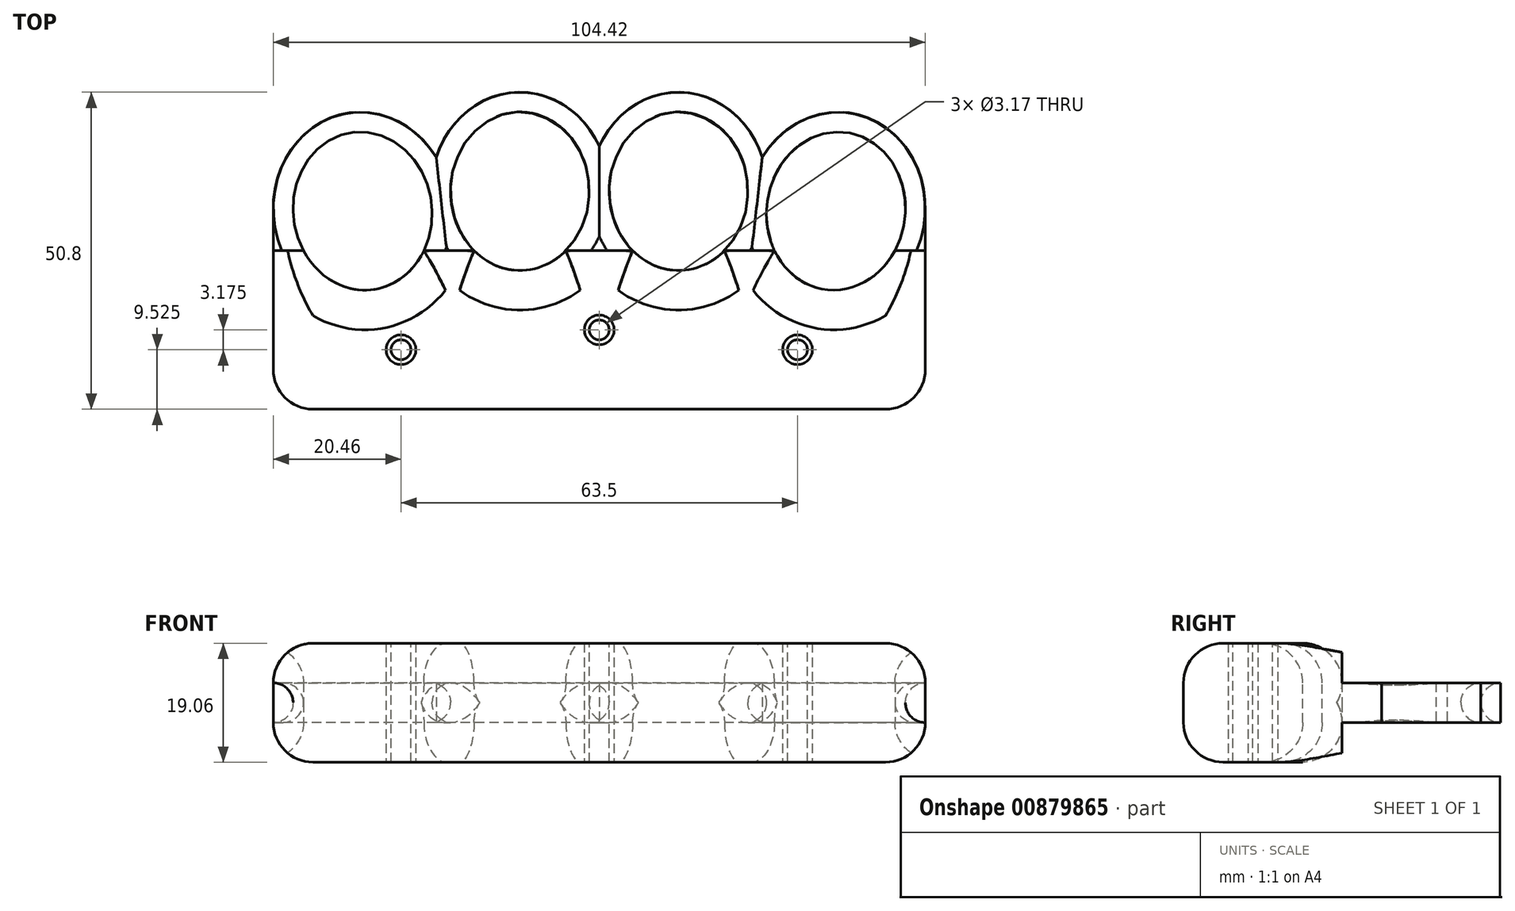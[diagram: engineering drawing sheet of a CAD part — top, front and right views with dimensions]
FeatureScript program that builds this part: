
annotation { "Feature Type Name" : "Feature", "Feature Type Description" : "" }
export const myFeature = defineFeature(function(context is Context, id is Id, definition is map)
    precondition{}
    {
        {
            var Q0;
            Q0=qCreatedBy(makeId("Top.planeOp"),FACE);
            var sketch = newSketch(context, id + "F0", { "sketchPlane" : qUnion([Q0])});
            skLineSegment(sketch, "E0.bottom", {"start": v(52.39, 0) * mm, "end": v(-52.39, 0) * mm});
            skLineSegment(sketch, "E0.top", {"start": v(52.39, 50.8) * mm, "end": v(-52.39, 50.8) * mm, "construction": true});
            skLineSegment(sketch, "E0.left", {"start": v(52.39, 0) * mm, "end": v(52.39, 50.8) * mm, "construction": true});
            skLineSegment(sketch, "E0.right", {"start": v(-52.39, 0) * mm, "end": v(-52.39, 50.8) * mm, "construction": true});
            skPoint(sketch, "E0.middle", {"position": v(0, 25.4) * mm});
            skEllipse(sketch, "E1", {"center": v(12.7, 34.93) * mm, "majorRadius": 12.7 * mm, "minorRadius": 11.11 * mm, "majorAxis": v(0, -1)});
            skEllipse(sketch, "E2", {"center": v(37.9, 31.75) * mm, "majorRadius": 12.7 * mm, "minorRadius": 11.11 * mm, "majorAxis": v(-0.13, -1)});
            skLineSegment(sketch, "E3", {"start": v(12.7, 34.93) * mm, "end": v(37.9, 31.75) * mm, "construction": true});
            skLineSegment(sketch, "E4", {"start": v(39.49, 44.35) * mm, "end": v(36.31, 19.15) * mm, "construction": true});
            skLineSegment(sketch, "E5", {"start": v(0, -19.1) * mm, "end": v(0, 88.95) * mm, "construction": true});
            skEllipticalArc(sketch, "E6", {});
            skEllipticalArc(sketch, "E7", {});
            skLineSegment(sketch, "E8", {"start": v(39.89, 47.5) * mm, "end": v(35.92, 16) * mm, "construction": true});
            skEllipticalArc(sketch, "E9.trimOffspring", {});
            skEllipticalArc(sketch, "E10.trimOffspring", {});
            skEllipticalArc(sketch, "E11.MirrorCS", {});
            skEllipse(sketch, "E12.MirrorC", {"center": v(-12.7, 34.93) * mm, "majorRadius": 12.7 * mm, "minorRadius": 11.11 * mm, "majorAxis": v(0, -1)});
            skEllipticalArc(sketch, "E13.MirrorCS", {});
            skEllipse(sketch, "E14.MirrorC", {"center": v(-37.9, 31.75) * mm, "majorRadius": 12.7 * mm, "minorRadius": 11.11 * mm, "majorAxis": v(0.13, -1)});
            skPoint(sketch, "E15.MirrorCS.end.orphan", {"position": v(-59.92, 0) * mm});
            skPoint(sketch, "E15.MirrorCS.start.orphan", {"position": v(-52.2, 31.75) * mm});
            skPoint(sketch, "E16.end.orphan", {"position": v(59.92, 0) * mm});
            skLineSegment(sketch, "E17", {"start": v(52.2, 31.75) * mm, "end": v(52.2, 0) * mm});
            skLineSegment(sketch, "E18", {"start": v(-52.2, 31.75) * mm, "end": v(-52.2, 0) * mm});
            skLineSegment(sketch, "E19.top", {"start": v(52.2, 0) * mm, "end": v(-52.2, 0) * mm, "construction": true});
            skLineSegment(sketch, "E19.left", {"start": v(52.2, 22.23) * mm, "end": v(52.2, 0) * mm, "construction": true});
            skLineSegment(sketch, "E19.right", {"start": v(-52.2, 22.23) * mm, "end": v(-52.2, 0) * mm, "construction": true});
            skPoint(sketch, "E19.middle", {"position": v(0, 11.11) * mm});
            skPoint(sketch, "E19.cornerSnap0", {"position": v(12.7, 22.23) * mm});
            skLineSegment(sketch, "E20", {"start": v(-52.2, 25.4) * mm, "end": v(-47.35, 25.4) * mm});
            skLineSegment(sketch, "E21", {"start": v(-28.08, 25.4) * mm, "end": v(-20.05, 25.4) * mm});
            skLineSegment(sketch, "E22", {"start": v(-5.35, 25.4) * mm, "end": v(5.35, 25.4) * mm});
            skLineSegment(sketch, "E23", {"start": v(20.05, 25.4) * mm, "end": v(28.08, 25.4) * mm});
            skLineSegment(sketch, "E24", {"start": v(47.35, 25.4) * mm, "end": v(52.2, 25.4) * mm});
            const initialGuessF0  = {"E6": [0.0127, 0.034925, 0, 1, 0.015875, 0.014287500000000002, 4.549107403088378, 4.626167916825997], "E7": [0.037900781237890244, 0.03175, -0.125, -0.9921567416492215, 0.015875, 0.014287500000000002, 1.6837034290787396, 4.24838283304531], "E9.trimOffspring": [0.037900781237890244, 0.03175, -0.125, -0.9921567416492215, 0.015875, 0.014287500000000002, 4.688269598477033, 4.765675536865148], "E10.trimOffspring": [0.0127, 0.034925, 0, 1, 0.015875, 0.014287500000000002, 5.064232675246107, 1.094914077134481], "E11.MirrorCS": [-0.0127, 0.034925, 0, 1, 0.015875, 0.014287500000000002, 5.188271230045105, 1.2189526319334796], "E13.MirrorCS": [-0.037900781237890244, 0.03175, 0.125, -0.9921567416492215, 0.015875, 0.014287500000000002, 2.034802474134276, 4.599481878100846]};
            skSetInitialGuess(sketch, initialGuessF0);
            skSolve(sketch);
        }
        {
            var Q0;
            {var subQ0=sQuery(id+"F0.wireOp",EDGE,"E7");Q0=makeQuery(id+"F0.imprint","IMPRINT",FACE,{"disambiguationData":[TD([[makeQuery(id+"F0.imprint","IMPRINT",EDGE,{"derivedFrom":subQ0}),1.0]])]});}
            var Q1;
            {var subQ3=sQuery(id+"F0.wireOp",EDGE,"E19.bottom");Q1=makeQuery(id+"F0.imprint","IMPRINT",FACE,{"disambiguationData":[TD([[makeQuery(id+"F0.imprint","IMPRINT",EDGE,{"derivedFrom":subQ3}),1.0]])]});}
            extrude(context, id + "F1", {"entities" : qUnion([Q0, Q1]), "depth" : 3.17 * mm, "offsetDistance" : 25.4 * mm, "hasSecondDirection" : true, "secondDirectionOppositeDirection" : true, "secondDirectionDepth" : 3.17 * mm});
        }
        {
            var Q0;
            {var subQ2=sQuery(id+"F0.wireOp",EDGE,"E20");Q0=makeQuery(id+"F0.imprint","IMPRINT",FACE,{"disambiguationData":[TD([[makeQuery(id+"F0.imprint","IMPRINT",EDGE,{"derivedFrom":subQ2}),-1.0]])]});}
            extrude(context, id + "F2", {"entities" : qUnion([Q0]), "operationType" : NewBodyOperationType.ADD, "depth" : 9.52 * mm, "offsetDistance" : 25.4 * mm, "hasSecondDirection" : true, "secondDirectionOppositeDirection" : true, "secondDirectionDepth" : 9.52 * mm});
        }
        {
            var Q0;
            Q0=makeQuery(id+"F2.opExtrude","CAP_FACE",FACE,{"disambiguationData":[OSD([sQuery(id+"F0.wireOp",EDGE,"E0.bottom"),sQuery(id+"F0.wireOp",EDGE,"E1"),sQuery(id+"F0.wireOp",EDGE,"E2"),sQuery(id+"F0.wireOp",EDGE,"E12.MirrorC"),sQuery(id+"F0.wireOp",EDGE,"E14.MirrorC"),sQuery(id+"F0.wireOp",EDGE,"E17"),sQuery(id+"F0.wireOp",EDGE,"E18"),sQuery(id+"F0.wireOp",EDGE,"E20"),sQuery(id+"F0.wireOp",EDGE,"E21"),sQuery(id+"F0.wireOp",EDGE,"E22"),sQuery(id+"F0.wireOp",EDGE,"E23"),sQuery(id+"F0.wireOp",EDGE,"E24")])],"isStart":false});
            var Q1;
            Q1=makeQuery(id+"F2.opExtrude","CAP_FACE",FACE,{"disambiguationData":[OSD([sQuery(id+"F0.wireOp",EDGE,"E0.bottom"),sQuery(id+"F0.wireOp",EDGE,"E1"),sQuery(id+"F0.wireOp",EDGE,"E2"),sQuery(id+"F0.wireOp",EDGE,"E12.MirrorC"),sQuery(id+"F0.wireOp",EDGE,"E14.MirrorC"),sQuery(id+"F0.wireOp",EDGE,"E17"),sQuery(id+"F0.wireOp",EDGE,"E18"),sQuery(id+"F0.wireOp",EDGE,"E20"),sQuery(id+"F0.wireOp",EDGE,"E21"),sQuery(id+"F0.wireOp",EDGE,"E22"),sQuery(id+"F0.wireOp",EDGE,"E23"),sQuery(id+"F0.wireOp",EDGE,"E24")])],"isStart":true});
            fillet(context, id + "F3", {"entities" : qUnion([Q0, Q1]), "radius" : 6.35 * mm, "tangentPropagation" : true, "allowEdgeOverflow" : false});
        }
        {
            var Q0;
            Q0=makeQuery(id+"F2.opExtrude","SWEPT_EDGE",EDGE,{"disambiguationData":[OSD([sQuery(id+"F0.wireOp",EDGE,"E0.bottom"),sQuery(id+"F0.wireOp",EDGE,"E17")])]});
            var Q1;
            Q1=makeQuery(id+"F2.opExtrude","SWEPT_EDGE",EDGE,{"disambiguationData":[OSD([sQuery(id+"F0.wireOp",EDGE,"E0.bottom"),sQuery(id+"F0.wireOp",EDGE,"E18")])]});
            fillet(context, id + "F4", {"entities" : qUnion([Q0, Q1]), "radius" : 6.35 * mm, "tangentPropagation" : true, "allowEdgeOverflow" : false});
        }
        {
            var Q0;
            Q0=qCreatedBy(makeId("Top.planeOp"),FACE);
            var sketch = newSketch(context, id + "F5", { "sketchPlane" : qUnion([Q0])});
            skCircle(sketch, "E25", {"center": v(0, 12.7) * mm, "radius": 1.59 * mm});
            skCircle(sketch, "E26", {"center": v(0, 12.7) * mm, "radius": 2.38 * mm});
            skCircle(sketch, "E27", {"center": v(31.75, 9.53) * mm, "radius": 1.59 * mm});
            skCircle(sketch, "E28", {"center": v(31.75, 9.53) * mm, "radius": 2.38 * mm});
            skCircle(sketch, "E29", {"center": v(-31.75, 9.52) * mm, "radius": 1.59 * mm});
            skCircle(sketch, "E30", {"center": v(-31.75, 9.52) * mm, "radius": 2.38 * mm});
            skSolve(sketch);
        }
        {
            var Q0;
            Q0=makeQuery(id+"F5.imprint","IMPRINT",FACE,{"disambiguationData":[TD([[makeQuery(id+"F5.imprint","IMPRINT",EDGE,{"derivedFrom":sQuery(id+"F5.wireOp",EDGE,"E25")}),1.0]])]});
            extrude(context, id + "F6", {"entities" : qUnion([Q0]), "operationType" : NewBodyOperationType.REMOVE, "oppositeDirection" : true, "depth" : 25.4 * mm, "offsetDistance" : 25.4 * mm, "hasSecondDirection" : true, "secondDirectionOppositeDirection" : false, "secondDirectionDepth" : 25.4 * mm});
        }
        {
            var Q0;
            Q0=makeQuery(id+"F5.imprint","IMPRINT",FACE,{"disambiguationData":[TD([[makeQuery(id+"F5.imprint","IMPRINT",EDGE,{"derivedFrom":sQuery(id+"F5.wireOp",EDGE,"E29")}),1.0]])]});
            var Q1;
            Q1=makeQuery(id+"F5.imprint","IMPRINT",FACE,{"disambiguationData":[TD([[makeQuery(id+"F5.imprint","IMPRINT",EDGE,{"derivedFrom":sQuery(id+"F5.wireOp",EDGE,"E27")}),1.0]])]});
            extrude(context, id + "F7", {"entities" : qUnion([Q0, Q1]), "operationType" : NewBodyOperationType.REMOVE, "oppositeDirection" : true, "depth" : 25.4 * mm, "offsetDistance" : 25.4 * mm, "hasSecondDirection" : true, "secondDirectionOppositeDirection" : false, "secondDirectionDepth" : 25.4 * mm});
        }
        {
            var Q0;
            Q0=makeQuery(id+"F5.imprint","IMPRINT",FACE,{"disambiguationData":[TD([[makeQuery(id+"F5.imprint","IMPRINT",EDGE,{"derivedFrom":sQuery(id+"F5.wireOp",EDGE,"E29")}),1.0]])]});
            var Q1;
            Q1=makeQuery(id+"F5.imprint","IMPRINT",FACE,{"disambiguationData":[TD([[makeQuery(id+"F5.imprint","IMPRINT",EDGE,{"derivedFrom":sQuery(id+"F5.wireOp",EDGE,"E29")}),-1.0]])]});
            var Q2;
            Q2=makeQuery(id+"F5.imprint","IMPRINT",FACE,{"disambiguationData":[TD([[makeQuery(id+"F5.imprint","IMPRINT",EDGE,{"derivedFrom":sQuery(id+"F5.wireOp",EDGE,"E25")}),1.0]])]});
            var Q3;
            Q3=makeQuery(id+"F5.imprint","IMPRINT",FACE,{"disambiguationData":[TD([[makeQuery(id+"F5.imprint","IMPRINT",EDGE,{"derivedFrom":sQuery(id+"F5.wireOp",EDGE,"E25")}),-1.0]])]});
            var Q4;
            Q4=makeQuery(id+"F5.imprint","IMPRINT",FACE,{"disambiguationData":[TD([[makeQuery(id+"F5.imprint","IMPRINT",EDGE,{"derivedFrom":sQuery(id+"F5.wireOp",EDGE,"E27")}),1.0]])]});
            var Q5;
            Q5=makeQuery(id+"F5.imprint","IMPRINT",FACE,{"disambiguationData":[TD([[makeQuery(id+"F5.imprint","IMPRINT",EDGE,{"derivedFrom":sQuery(id+"F5.wireOp",EDGE,"E27")}),-1.0]])]});
            extrude(context, id + "F8", {"entities" : qUnion([Q0, Q1, Q2, Q3, Q4, Q5]), "depth" : 9.52 * mm, "offsetDistance" : 25.4 * mm, "hasSecondDirection" : true, "secondDirectionOppositeDirection" : true, "secondDirectionDepth" : 9.52 * mm});
        }
        {
            var Q0;
            Q0=makeQuery(id+"F1.opExtrude","CAP_EDGE",EDGE,{"disambiguationData":[OSD([sQuery(id+"F0.wireOp",EDGE,"E14.MirrorC")])],"isStart":true});
            var Q1;
            Q1=makeQuery(id+"F1.opExtrude","CAP_EDGE",EDGE,{"disambiguationData":[OSD([sQuery(id+"F0.wireOp",EDGE,"E12.MirrorC")])],"isStart":true});
            var Q2;
            Q2=makeQuery(id+"F1.opExtrude","CAP_EDGE",EDGE,{"disambiguationData":[OSD([sQuery(id+"F0.wireOp",EDGE,"E1")])],"isStart":true});
            var Q3;
            Q3=makeQuery(id+"F1.opExtrude","CAP_EDGE",EDGE,{"disambiguationData":[OSD([sQuery(id+"F0.wireOp",EDGE,"E2")])],"isStart":true});
            var Q4;
            Q4=makeQuery(id+"F1.opExtrude","CAP_EDGE",EDGE,{"disambiguationData":[OSD([sQuery(id+"F0.wireOp",EDGE,"E14.MirrorC")])],"isStart":false});
            var Q5;
            Q5=makeQuery(id+"F1.opExtrude","CAP_EDGE",EDGE,{"disambiguationData":[OSD([sQuery(id+"F0.wireOp",EDGE,"E12.MirrorC")])],"isStart":false});
            var Q6;
            Q6=makeQuery(id+"F1.opExtrude","CAP_EDGE",EDGE,{"disambiguationData":[OSD([sQuery(id+"F0.wireOp",EDGE,"E1")])],"isStart":false});
            var Q7;
            Q7=makeQuery(id+"F1.opExtrude","CAP_EDGE",EDGE,{"disambiguationData":[OSD([sQuery(id+"F0.wireOp",EDGE,"E2")])],"isStart":false});
            fillet(context, id + "F9", {"entities" : qUnion([Q0, Q1, Q2, Q3, Q4, Q5, Q6, Q7]), "radius" : 3.15 * mm, "tangentPropagation" : true, "allowEdgeOverflow" : false});
        }
    });
